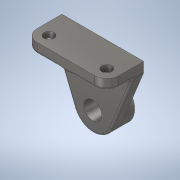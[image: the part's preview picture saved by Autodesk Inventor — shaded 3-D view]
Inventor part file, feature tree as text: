
AUTODESK INVENTOR PART (.ipt)
format: ipt  version: 2020 (Build 240168000, 168)  size: 422,400 bytes
history: native  units: mm
features: extrude x5, sketch x4, fillet x2, plane x1, rib x1
ambient origin geometry x8: Origin, YZ Plane, XZ Plane, XY Plane, X Axis, Y Axis, Z Axis, Center Point
bodies: Solid1 (feature_tree)
feature tree (13):
  extrude  "Extrusion1"  Depth=41.0mm
  sketch  "Sketch2"  dims[d2=18.0mm d3=22.0mm d4=0.0mm]
  extrude  "Extrusion2"  Depth=22.0mm TaperAngle=0.0deg
  extrude  "Extrusion3"  Depth=41.0mm
  plane  "Work Plane1"
  rib  "Rib1"
  sketch  "Sketch6"  dims[d7=10.0mm d8=10.0mm d9=0.0mm d10=27.0mm d11=0.0mm d12=-41.0mm d17=1.0mm d18=10.0mm d19=0.0mm d20=0.0mm d21=1.0mm d22=1.0mm d23=10.0mm d24=22.0mm d25=22.0mm d26=10.0mm d27=12.0mm d28=12.0mm d29=12.0mm d30=12.0mm d31=27.0mm d32=0.0mm d33=4.0mm d34=0.0mm d35=12.0mm d37=2.0mm]
  extrude  "Extrusion4"  Depth=10.0mm TaperAngle=0.0deg
  extrude  "Extrusion5"  Depth=27.0mm TaperAngle=0.0deg
  fillet  "Fillet1"  [1 undecoded]
  fillet  "Fillet3"  Radius=1.0mm
  sketch  "Sketch1"  dims[d0=40.0mm d1=41.0mm]
  sketch  "Sketch5"  dims[d5=82.0mm d6=41.0mm]
note: 1 required parameter value undecoded (feature->parameter linkage not recoverable at this tier; creation-order binding heuristic only, values carry confidence <= 0.55)
